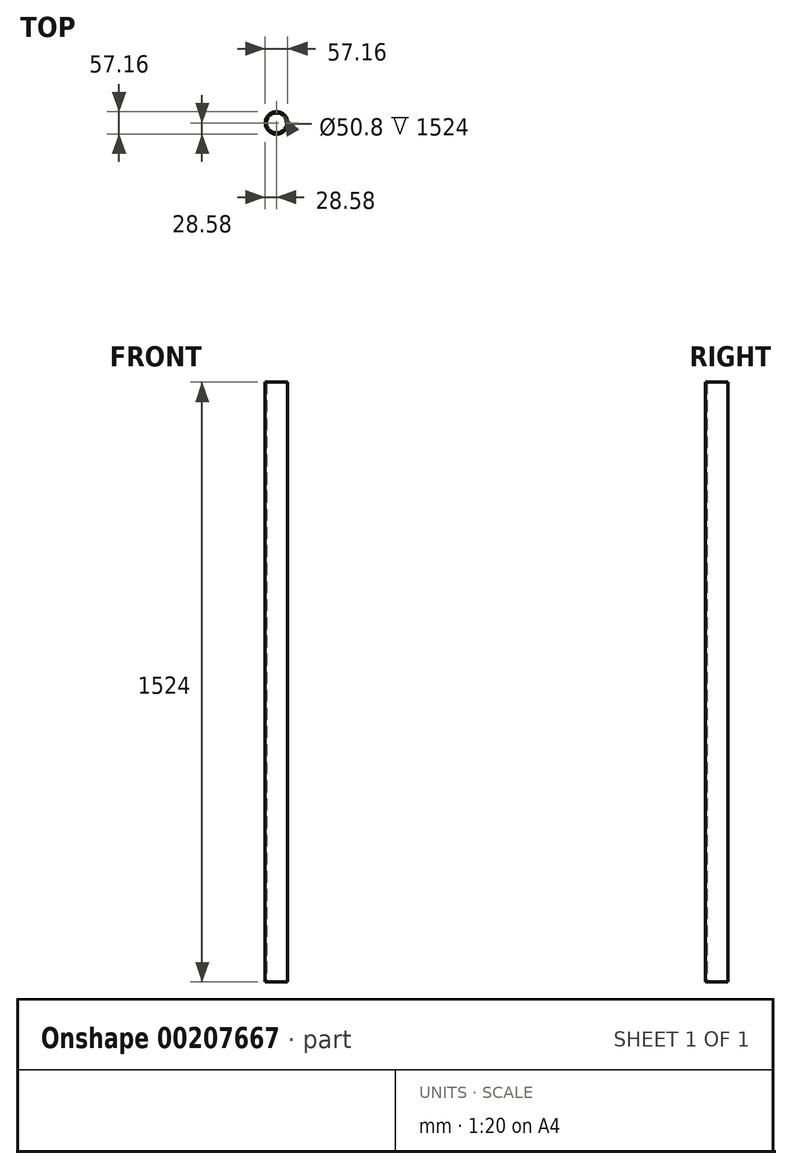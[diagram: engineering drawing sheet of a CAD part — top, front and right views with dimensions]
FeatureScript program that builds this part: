
annotation { "Feature Type Name" : "Feature", "Feature Type Description" : "" }
export const myFeature = defineFeature(function(context is Context, id is Id, definition is map)
    precondition{}
    {
        {
            var Q0;
            Q0=qCreatedBy(makeId("Top.planeOp"),FACE);
            var sketch = newSketch(context, id + "F0", { "sketchPlane" : qUnion([Q0])});
            skCircle(sketch, "E0", {"center": v(0, 0) * mm, "radius": 28.58 * mm});
            skCircle(sketch, "E1", {"center": v(0, 0) * mm, "radius": 25.4 * mm});
            skSolve(sketch);
        }
        {
            var Q0;
            Q0=makeQuery(id+"F0.imprint","IMPRINT",FACE,{"disambiguationData":[TD([[makeQuery(id+"F0.imprint","IMPRINT",EDGE,{"derivedFrom":sQuery(id+"F0.wireOp",EDGE,"E0")}),1.0]])]});
            extrude(context, id + "F1", {"entities" : qUnion([Q0]), "depth" : 1524 * mm});
        }
    });
